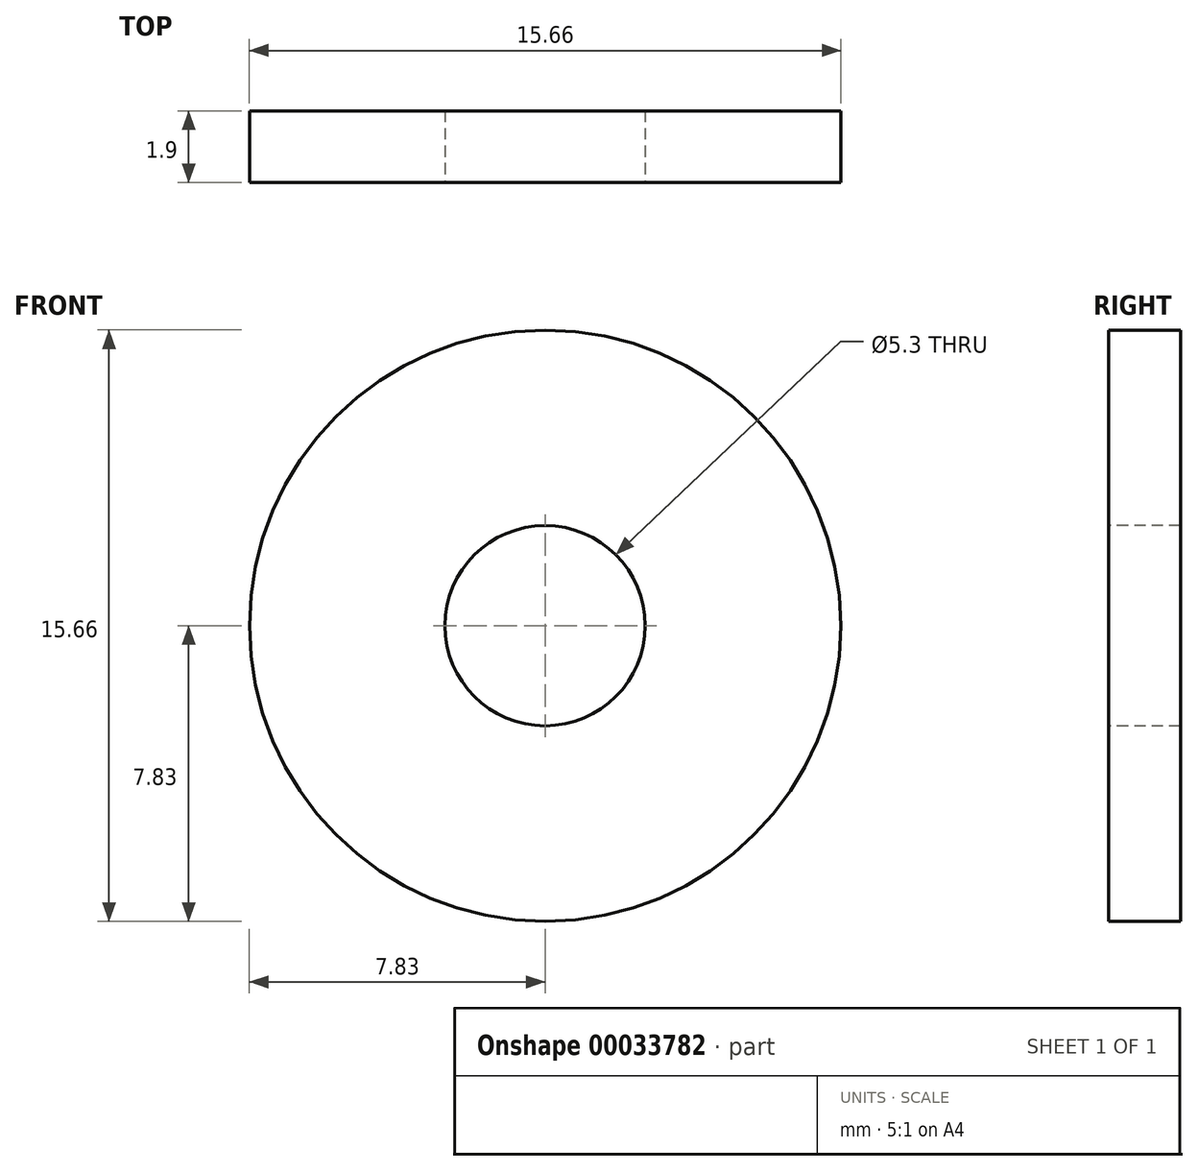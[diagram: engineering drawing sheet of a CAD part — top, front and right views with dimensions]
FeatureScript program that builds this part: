
annotation { "Feature Type Name" : "Feature", "Feature Type Description" : "" }
export const myFeature = defineFeature(function(context is Context, id is Id, definition is map)
    precondition{}
    {
        {
            var Q0;
            Q0=qCreatedBy(makeId("Front.planeOp"),FACE);
            var sketch = newSketch(context, id + "F0", { "sketchPlane" : qUnion([Q0])});
            skCircle(sketch, "E0", {"center": v(0, 0) * mm, "radius": 7.83 * mm});
            skCircle(sketch, "E1", {"center": v(0, 0) * mm, "radius": 2.65 * mm});
            skSolve(sketch);
        }
        {
            var Q0;
            Q0=makeQuery(id+"F0.imprint","IMPRINT",FACE,{"disambiguationData":[TD([[makeQuery(id+"F0.imprint","IMPRINT",EDGE,{"derivedFrom":sQuery(id+"F0.wireOp",EDGE,"E0")}),1.0]])]});
            extrude(context, id + "F1", {"entities" : qUnion([Q0]), "oppositeDirection" : true, "depth" : 1.9 * mm});
        }
    });
